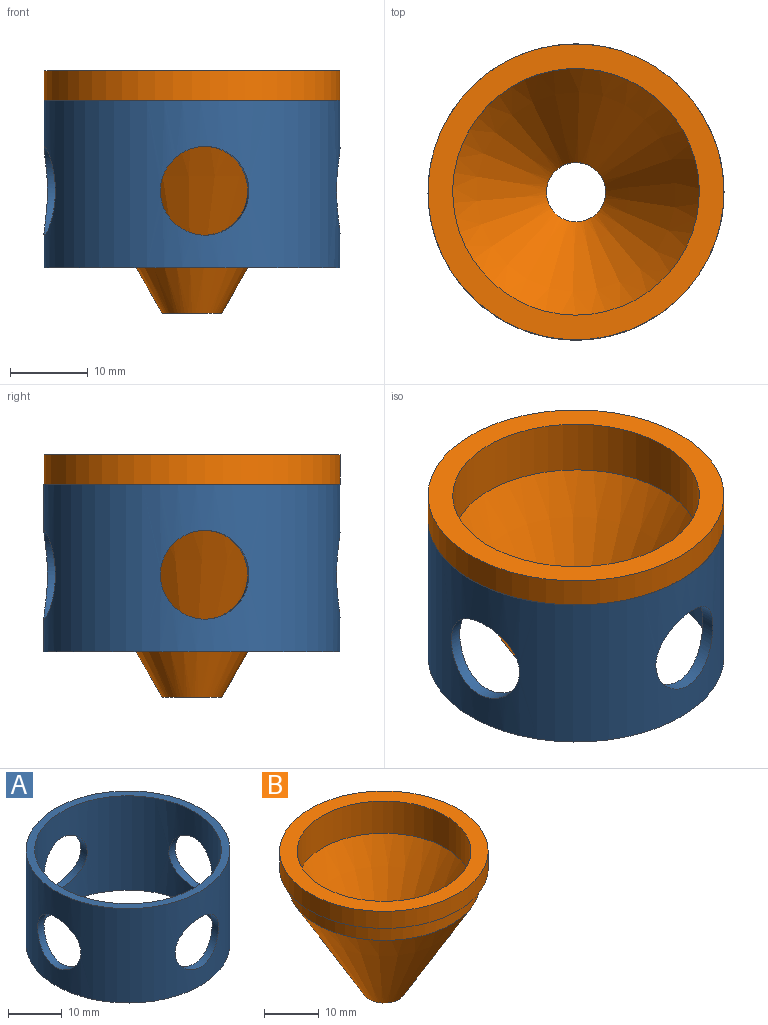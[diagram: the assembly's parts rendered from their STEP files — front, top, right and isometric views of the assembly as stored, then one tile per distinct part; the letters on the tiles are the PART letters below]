
ASSEMBLY  parts=2 mates=1
PART A: 8 faces, bbox 38.1x38.1x21.6 mm
  f0: cylinder r=17.46mm len=34.93mm, axis (0,0,-1), area 1953mm2, adj f2,f3,f4,f5,f6,f7
  f1: cylinder r=19.05mm len=38.1mm, axis (0,0,-1), area 2169.1mm2, adj f2,f3,f4,f5,f6,f7
  f2: plane 38.1x38.1mm, normal (0,0,1), area 182.1mm2, adj f0,f1
  f3: plane 38.1x38.1mm, normal (0,0,-1), area 182.1mm2, adj f0,f1
  f4: cylinder r=5.71mm len=11.43mm, axis (0,-1,0), area 58.5mm2, adj f0,f1
  f5: cylinder r=5.71mm len=11.43mm, axis (0,-1,0), area 58.5mm2, adj f0,f1
  f6: cylinder r=5.71mm len=11.43mm, axis (-1,0,0), area 58.5mm2, adj f0,f1
  f7: cylinder r=5.71mm len=11.43mm, axis (-1,0,0), area 58.5mm2, adj f0,f1
PART B: 8 faces, bbox 38.1x38.1x31.3 mm
  f0: plane 38.1x38.1mm, normal (0,0,1), area 348.4mm2, adj f1,f7
  f1: cylinder r=15.88mm len=31.75mm, axis (0,0,-1), area 717.6mm2, adj f0,f2
  f2: cone r=3.81mm half-angle=30deg, axis (0,0,1), area 1492.3mm2, adj f1,f3
  f3: cylinder r=3.81mm len=7.62mm, axis (0,0,-1), area 76mm2, adj f2,f4
  f4: cone r=17.46mm half-angle=30deg, axis (0,0,1), area 1824.8mm2, adj f3,f5
  f5: cylinder r=17.46mm len=34.93mm, axis (0,0,-1), area 418mm2, adj f4,f6
  f6: plane 38.1x38.1mm, normal (0,0,-1), area 182.1mm2, adj f5,f7
  f7: cylinder r=19.05mm len=38.1mm, axis (0,0,-1), area 456mm2, adj f0,f6
PLACE A rot(axis=(0,0,1),5.1deg) t=(0,0,-16.47)mm
PLACE B rot(axis=(0,0,1),5.1deg) t=(0,0,-20.28)mm
MATE fastened B.f1 <-> A.f0  axis (0,0,-1) through (0,0,5.12)mm
